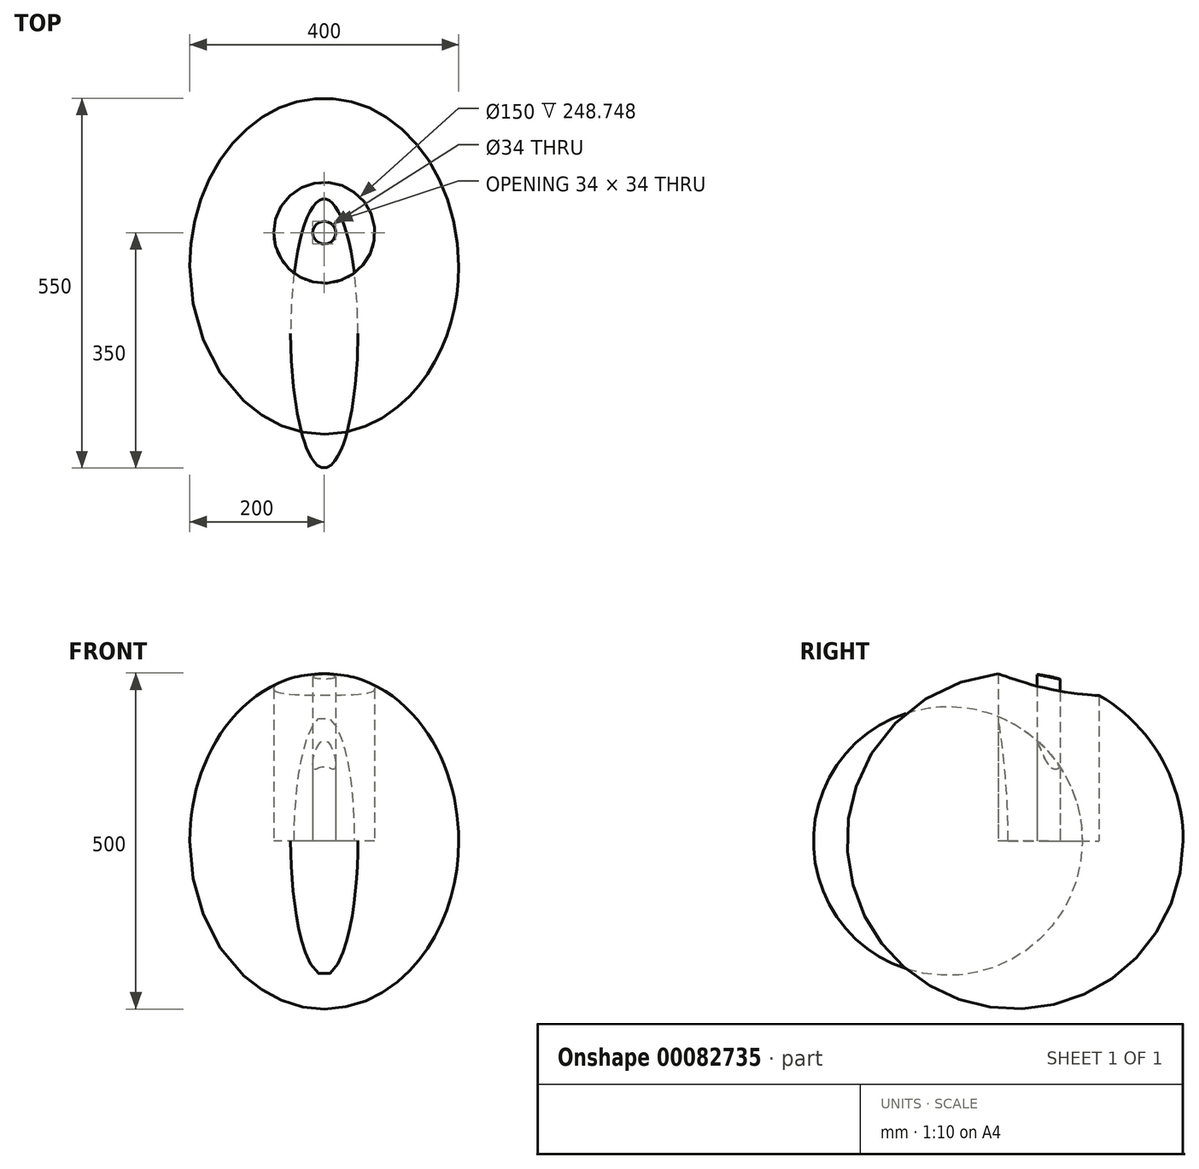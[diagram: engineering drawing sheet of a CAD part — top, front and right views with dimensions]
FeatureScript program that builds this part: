
annotation { "Feature Type Name" : "Feature", "Feature Type Description" : "" }
export const myFeature = defineFeature(function(context is Context, id is Id, definition is map)
    precondition{}
    {
        {
            var Q0;
            Q0=qCreatedBy(makeId("Top.planeOp"),FACE);
            var sketch = newSketch(context, id + "F0", { "sketchPlane" : qUnion([Q0])});
            skEllipticalArc(sketch, "E0", {});
            skLineSegment(sketch, "E1", {"start": v(0, 0) * mm, "end": v(0, 200) * mm});
            skLineSegment(sketch, "E2", {"start": v(0, 0) * mm, "end": v(50, 0) * mm});
            skPoint(sketch, "E3.end.orphan", {"position": v(0, -200) * mm});
            skLineSegment(sketch, "E4", {"start": v(0, 0) * mm, "end": v(106.97, 0) * mm});
            skEllipticalArc(sketch, "E5.MirrorCS", {});
            skLineSegment(sketch, "E6.MirrorCS", {"start": v(0, 0) * mm, "end": v(-106.97, 0) * mm});
            const initialGuessF0  = {"E0": [0, 0, 0, -1, 0.2, 0.05, 1.5707963267948966, 3.141592653589793], "E5.MirrorCS": [0, 0, 0, -1, 0.2, 0.05, 3.141592653589793, 4.71238898038469]};
            skSetInitialGuess(sketch, initialGuessF0);
            skSolve(sketch);
        }
        {
            var Q0;
            {var subQ0=sQuery(id+"F0.wireOp",EDGE,"E0");Q0=makeQuery(id+"F0.imprint","IMPRINT",FACE,{"disambiguationData":[TD([[makeQuery(id+"F0.imprint","IMPRINT",EDGE,{"derivedFrom":subQ0}),1.0]])]});}
            var Q1;
            {var subQ0=sQuery(id+"F0.wireOp",EDGE,"E1");Q1=makeQuery(id+"F0.imprint","IMPRINT",FACE,{"disambiguationData":[TD([[makeQuery(id+"F0.imprint","IMPRINT",EDGE,{"derivedFrom":subQ0}),1.0]])]});}
            var Q2;
            Q2=sQuery(id+"F0.wireOp",EDGE,"E4");
            revolve(context, id + "F1", {"entities" : qUnion([Q0, Q1]), "axis" : qUnion([Q2]), "revolveType" : RevolveType.FULL});
        }
        {
            var Q0;
            Q0=qCreatedBy(makeId("Top.planeOp"),FACE);
            var sketch = newSketch(context, id + "F2", { "sketchPlane" : qUnion([Q0])});
            skLineSegment(sketch, "E7", {"start": v(0, 0) * mm, "end": v(0, 270.2) * mm});
            skLineSegment(sketch, "E8", {"start": v(0, 270.2) * mm, "end": v(0, 0) * mm});
            skEllipticalArc(sketch, "E9", {});
            skLineSegment(sketch, "E10", {"start": v(0, 100) * mm, "end": v(200, 100) * mm});
            skLineSegment(sketch, "E11", {"start": v(0, 100) * mm, "end": v(-175.48, 100) * mm});
            skLineSegment(sketch, "E12", {"start": v(200, 100) * mm, "end": v(307.18, 100) * mm, "construction": true});
            skLineSegment(sketch, "E13", {"start": v(-175.48, 100) * mm, "end": v(-234.96, 100) * mm});
            const initialGuessF2  = {"E9": [0, 0.1, 1, 0, 0.2, 0.25, 6.283185307179586, 3.141592653589793]};
            skSetInitialGuess(sketch, initialGuessF2);
            skSolve(sketch);
        }
        {
            var Q0;
            {var subQ0=sQuery(id+"F2.wireOp",EDGE,"E9");Q0=makeQuery(id+"F2.imprint","IMPRINT",FACE,{"disambiguationData":[TD([[makeQuery(id+"F2.imprint","IMPRINT",EDGE,{"derivedFrom":subQ0}),1.0]])]});}
            var Q1;
            Q1=sQuery(id+"F2.wireOp",EDGE,"E12");
            revolve(context, id + "F3", {"entities" : qUnion([Q0]), "axis" : qUnion([Q1]), "revolveType" : RevolveType.FULL});
        }
        {
            var Q0;
            Q0=qCreatedBy(makeId("Right.planeOp"),FACE);
            cPlane(context, id + "F4", {"entities" : qUnion([Q0]), "cplaneType" : CPlaneType.OFFSET, "offset" : 110 * mm, "width" : 150 * mm, "height" : 150 * mm});
        }
        {
            var Q0;
            Q0=qCreatedBy(makeId("Top.planeOp"),FACE);
            var sketch = newSketch(context, id + "F5", { "sketchPlane" : qUnion([Q0])});
            skLineSegment(sketch, "E14", {"start": v(0, 0) * mm, "end": v(0, 449.65) * mm});
            skCircle(sketch, "E15", {"center": v(0, 150) * mm, "radius": 75 * mm});
            skCircle(sketch, "E16.0", {"center": v(0, 150) * mm, "radius": 76 * mm});
            skCircle(sketch, "E17.0", {"center": v(0, 150) * mm, "radius": 16 * mm});
            skCircle(sketch, "E18.0", {"center": v(0, 150) * mm, "radius": 17 * mm});
            skSolve(sketch);
        }
        {
            var Q0;
            {var subQ0=sQuery(id+"F5.wireOp",EDGE,"E16.0");var subQ1=sQuery(id+"F5.wireOp",EDGE,"E14");var subQ2=makeQuery(id+"F5.imprint","INTERSECT",VERTEX,{"disambiguationData":[OD(0.0)],"derivedFrom":[subQ1,subQ0]});Q0=makeQuery(id+"F5.imprint","IMPRINT",FACE,{"disambiguationData":[TD([[makeQuery(id+"F5.imprint","IMPRINT",EDGE,{"disambiguationData":[TD([[subQ2,-1.0]])],"derivedFrom":subQ1}),1.0]])]});}
            var Q1;
            {var subQ0=sQuery(id+"F5.wireOp",EDGE,"E16.0");var subQ1=sQuery(id+"F5.wireOp",EDGE,"E14");var subQ2=makeQuery(id+"F5.imprint","INTERSECT",VERTEX,{"disambiguationData":[OD(0.0)],"derivedFrom":[subQ1,subQ0]});Q1=makeQuery(id+"F5.imprint","IMPRINT",FACE,{"disambiguationData":[TD([[makeQuery(id+"F5.imprint","IMPRINT",EDGE,{"disambiguationData":[TD([[subQ2,-1.0]])],"derivedFrom":subQ1}),-1.0]])]});}
            var Q2;
            {var subQ0=sQuery(id+"F5.wireOp",EDGE,"E18.0");var subQ1=sQuery(id+"F5.wireOp",EDGE,"E14");var subQ2=makeQuery(id+"F5.imprint","INTERSECT",VERTEX,{"disambiguationData":[OD(0.0)],"derivedFrom":[subQ1,subQ0]});Q2=makeQuery(id+"F5.imprint","IMPRINT",FACE,{"disambiguationData":[TD([[makeQuery(id+"F5.imprint","IMPRINT",EDGE,{"disambiguationData":[TD([[subQ2,-1.0]])],"derivedFrom":subQ1}),-1.0]])]});}
            var Q3;
            {var subQ0=sQuery(id+"F5.wireOp",EDGE,"E18.0");var subQ1=sQuery(id+"F5.wireOp",EDGE,"E14");var subQ2=makeQuery(id+"F5.imprint","INTERSECT",VERTEX,{"disambiguationData":[OD(0.0)],"derivedFrom":[subQ1,subQ0]});Q3=makeQuery(id+"F5.imprint","IMPRINT",FACE,{"disambiguationData":[TD([[makeQuery(id+"F5.imprint","IMPRINT",EDGE,{"disambiguationData":[TD([[subQ2,-1.0]])],"derivedFrom":subQ1}),1.0]])]});}
            extrude(context, id + "F6", {"entities" : qUnion([Q0, Q1, Q2, Q3]), "operationType" : NewBodyOperationType.REMOVE, "endBound" : BoundingType.THROUGH_ALL, "depth" : 25 * mm});
        }
    });
